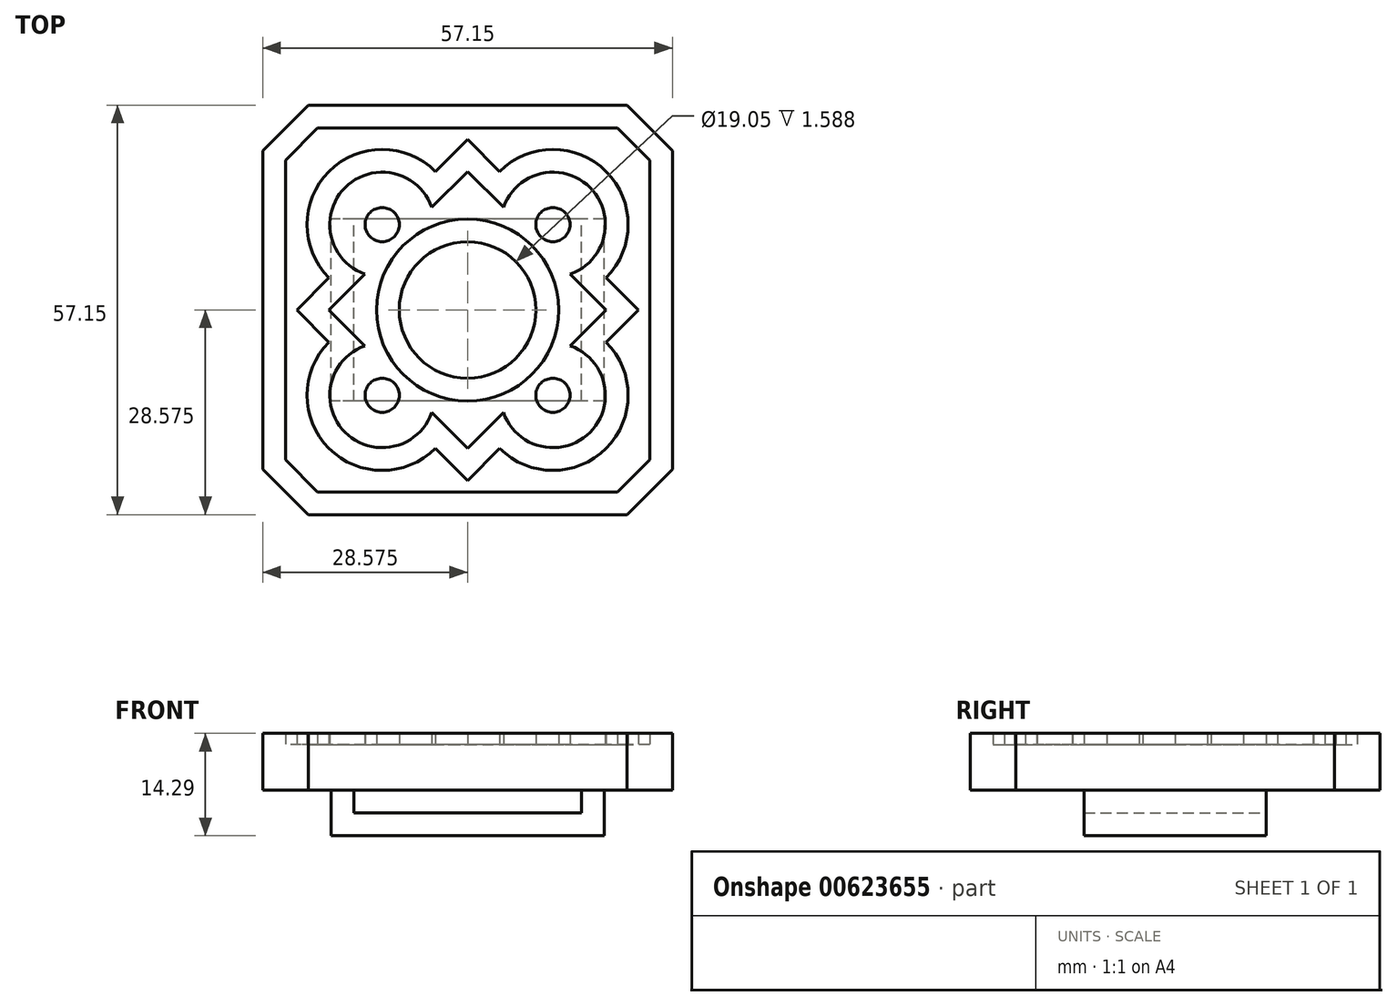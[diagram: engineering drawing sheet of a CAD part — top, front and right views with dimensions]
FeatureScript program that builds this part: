
annotation { "Feature Type Name" : "Feature", "Feature Type Description" : "" }
export const myFeature = defineFeature(function(context is Context, id is Id, definition is map)
    precondition{}
    {
        {
            var Q0;
            Q0=qCreatedBy(makeId("Top.planeOp"),FACE);
            var sketch = newSketch(context, id + "F0", { "sketchPlane" : qUnion([Q0])});
            skLineSegment(sketch, "E0.bottom", {"start": v(-57.15, 0) * mm, "end": v(0, 0) * mm, "construction": true});
            skLineSegment(sketch, "E0.top", {"start": v(-57.15, -57.15) * mm, "end": v(0, -57.15) * mm, "construction": true});
            skLineSegment(sketch, "E0.left", {"start": v(-57.15, 0) * mm, "end": v(-57.15, -57.15) * mm, "construction": true});
            skLineSegment(sketch, "E0.right", {"start": v(0, 0) * mm, "end": v(0, -57.15) * mm, "construction": true});
            skLineSegment(sketch, "E1", {"start": v(-50.8, 0) * mm, "end": v(-6.35, 0) * mm});
            skLineSegment(sketch, "E2", {"start": v(0, -6.35) * mm, "end": v(0, -50.8) * mm});
            skLineSegment(sketch, "E3", {"start": v(-57.15, -6.35) * mm, "end": v(-57.15, -50.8) * mm});
            skLineSegment(sketch, "E4", {"start": v(-50.8, -57.15) * mm, "end": v(-6.35, -57.15) * mm});
            skPoint(sketch, "E5", {"position": v(-28.58, 0) * mm});
            skPoint(sketch, "E6", {"position": v(-57.15, -28.57) * mm});
            skPoint(sketch, "E7", {"position": v(-28.58, -57.15) * mm});
            skPoint(sketch, "E8", {"position": v(0, -28.58) * mm});
            skLineSegment(sketch, "E9", {"start": v(-50.8, -57.15) * mm, "end": v(-57.15, -50.8) * mm});
            skLineSegment(sketch, "E10", {"start": v(0, -50.8) * mm, "end": v(-6.35, -57.15) * mm});
            skLineSegment(sketch, "E11", {"start": v(-57.15, -6.35) * mm, "end": v(-50.8, 0) * mm});
            skLineSegment(sketch, "E12", {"start": v(-6.35, 0) * mm, "end": v(0, -6.35) * mm});
            skLineSegment(sketch, "E13", {"start": v(-28.58, 0) * mm, "end": v(-28.58, -57.15) * mm, "construction": true});
            skPoint(sketch, "E14", {"position": v(-28.58, -28.58) * mm});
            skSolve(sketch);
        }
        {
            var Q0;
            Q0 = qSketchRegion(id + "F0", true);
            extrude(context, id + "F1", {"entities" : qUnion([Q0]), "depth" : 6.35 * mm, "offsetDistance" : 25.4 * mm});
        }
        {
            var Q0;
            Q0=makeQuery(id+"F1.opExtrude","CAP_FACE",FACE,{"disambiguationData":[OSD([sQuery(id+"F0.wireOp",EDGE,"E1"),sQuery(id+"F0.wireOp",EDGE,"E2"),sQuery(id+"F0.wireOp",EDGE,"E3"),sQuery(id+"F0.wireOp",EDGE,"E4"),sQuery(id+"F0.wireOp",EDGE,"E9"),sQuery(id+"F0.wireOp",EDGE,"E10"),sQuery(id+"F0.wireOp",EDGE,"E11"),sQuery(id+"F0.wireOp",EDGE,"E12")])],"isStart":false});
            var sketch = newSketch(context, id + "F2", { "sketchPlane" : qUnion([Q0])});
            skLineSegment(sketch, "E15", {"start": v(0, -28.58) * mm, "end": v(-57.15, -28.58) * mm, "construction": true});
            skCircle(sketch, "E16", {"center": v(-28.58, -28.58) * mm, "radius": 12.7 * mm});
            skCircle(sketch, "E17", {"center": v(-28.58, -28.58) * mm, "radius": 9.53 * mm});
            skLineSegment(sketch, "E18", {"start": v(-6.35, 0) * mm, "end": v(-50.8, 0) * mm});
            skLineSegment(sketch, "E19", {"start": v(0, -50.8) * mm, "end": v(-6.35, -57.15) * mm});
            skLineSegment(sketch, "E20", {"start": v(0, -50.8) * mm, "end": v(0, -6.35) * mm});
            skLineSegment(sketch, "E21", {"start": v(0, -6.35) * mm, "end": v(-6.35, 0) * mm});
            skLineSegment(sketch, "E22", {"start": v(-57.15, -6.35) * mm, "end": v(-50.8, 0) * mm});
            skLineSegment(sketch, "E23", {"start": v(-57.15, -50.8) * mm, "end": v(-50.8, -57.15) * mm});
            skLineSegment(sketch, "E24", {"start": v(-57.15, -6.35) * mm, "end": v(-57.15, -50.8) * mm});
            skLineSegment(sketch, "E25", {"start": v(-6.35, -57.15) * mm, "end": v(-50.8, -57.15) * mm});
            skLineSegment(sketch, "E26", {"start": v(-3.18, -49.48) * mm, "end": v(-3.18, -7.67) * mm});
            skLineSegment(sketch, "E27", {"start": v(-53.97, -49.48) * mm, "end": v(-53.97, -7.67) * mm});
            skLineSegment(sketch, "E28", {"start": v(-49.48, -53.98) * mm, "end": v(-7.67, -53.98) * mm});
            skLineSegment(sketch, "E29", {"start": v(-49.48, -3.17) * mm, "end": v(-7.67, -3.17) * mm});
            skLineSegment(sketch, "E30", {"start": v(-3.17, -7.67) * mm, "end": v(-7.67, -3.18) * mm});
            skLineSegment(sketch, "E31", {"start": v(-49.48, -53.97) * mm, "end": v(-53.97, -49.48) * mm});
            skLineSegment(sketch, "E32", {"start": v(-7.67, -53.97) * mm, "end": v(-3.17, -49.48) * mm});
            skLineSegment(sketch, "E33", {"start": v(-53.97, -7.67) * mm, "end": v(-49.48, -3.18) * mm});
            skLineSegment(sketch, "E34", {"start": v(-28.58, -53.98) * mm, "end": v(-28.58, -3.18) * mm, "construction": true});
            skLineSegment(sketch, "E35", {"start": v(-3.17, -3.18) * mm, "end": v(-53.98, -53.98) * mm, "construction": true});
            skLineSegment(sketch, "E36", {"start": v(-53.98, -3.17) * mm, "end": v(-3.17, -53.98) * mm, "construction": true});
            skLineSegment(sketch, "E37", {"start": v(-4.76, -28.58) * mm, "end": v(-28.58, -4.76) * mm, "construction": true});
            skLineSegment(sketch, "E38", {"start": v(-4.76, -28.57) * mm, "end": v(-28.57, -52.39) * mm, "construction": true});
            skLineSegment(sketch, "E39", {"start": v(-28.57, -52.39) * mm, "end": v(-52.39, -28.58) * mm, "construction": true});
            skLineSegment(sketch, "E40", {"start": v(-28.58, -4.76) * mm, "end": v(-52.39, -28.57) * mm, "construction": true});
            skCircle(sketch, "E41", {"center": v(-16.67, -40.48) * mm, "radius": 2.38 * mm});
            skCircle(sketch, "E42", {"center": v(-40.48, -40.48) * mm, "radius": 2.38 * mm});
            skCircle(sketch, "E43", {"center": v(-16.67, -16.67) * mm, "radius": 2.38 * mm});
            skCircle(sketch, "E44", {"center": v(-40.48, -16.67) * mm, "radius": 2.38 * mm});
            skLineSegment(sketch, "E45", {"start": v(-47.9, -28.58) * mm, "end": v(-28.58, -47.9) * mm, "construction": true});
            skLineSegment(sketch, "E46", {"start": v(-47.9, -28.58) * mm, "end": v(-28.58, -9.25) * mm, "construction": true});
            skLineSegment(sketch, "E47", {"start": v(-28.58, -9.25) * mm, "end": v(-9.25, -28.57) * mm, "construction": true});
            skLineSegment(sketch, "E48", {"start": v(-9.25, -28.57) * mm, "end": v(-28.58, -47.9) * mm, "construction": true});
            skArc(sketch, "E49", {"start": v(-24.08, -47.9) * mm, "mid": v(-9.25, -47.9) * mm, "end": v(-9.25, -33.07) * mm});
            skLineSegment(sketch, "E50", {"start": v(-9.25, -33.07) * mm, "end": v(-24.08, -47.9) * mm, "construction": true});
            skArc(sketch, "E51", {"start": v(-47.9, -33.07) * mm, "mid": v(-47.9, -47.9) * mm, "end": v(-33.07, -47.9) * mm});
            skArc(sketch, "E52", {"start": v(-33.07, -9.25) * mm, "mid": v(-47.9, -9.25) * mm, "end": v(-47.9, -24.08) * mm});
            skArc(sketch, "E53", {"start": v(-9.25, -24.08) * mm, "mid": v(-9.25, -9.25) * mm, "end": v(-24.08, -9.25) * mm});
            skLineSegment(sketch, "E54", {"start": v(-24.08, -47.9) * mm, "end": v(-28.57, -52.39) * mm});
            skLineSegment(sketch, "E55", {"start": v(-28.57, -52.39) * mm, "end": v(-33.07, -47.9) * mm});
            skLineSegment(sketch, "E56", {"start": v(-47.9, -33.07) * mm, "end": v(-52.39, -28.58) * mm});
            skLineSegment(sketch, "E57", {"start": v(-52.39, -28.58) * mm, "end": v(-47.9, -24.08) * mm});
            skLineSegment(sketch, "E58", {"start": v(-33.07, -9.25) * mm, "end": v(-28.58, -4.76) * mm});
            skLineSegment(sketch, "E59", {"start": v(-24.08, -9.25) * mm, "end": v(-28.58, -4.76) * mm});
            skLineSegment(sketch, "E60", {"start": v(-9.25, -24.08) * mm, "end": v(-4.76, -28.57) * mm});
            skLineSegment(sketch, "E61", {"start": v(-9.25, -33.07) * mm, "end": v(-4.76, -28.57) * mm});
            skArc(sketch, "E62", {"start": v(-14.26, -23.57) * mm, "mid": v(-11.5, -11.5) * mm, "end": v(-23.57, -14.26) * mm});
            skArc(sketch, "E63", {"start": v(-23.57, -42.9) * mm, "mid": v(-11.5, -45.65) * mm, "end": v(-14.26, -33.58) * mm});
            skArc(sketch, "E64", {"start": v(-42.9, -33.58) * mm, "mid": v(-45.65, -45.65) * mm, "end": v(-33.58, -42.9) * mm});
            skArc(sketch, "E65", {"start": v(-33.58, -14.26) * mm, "mid": v(-45.65, -11.5) * mm, "end": v(-42.9, -23.57) * mm});
            skLineSegment(sketch, "E66", {"start": v(-33.58, -42.9) * mm, "end": v(-28.58, -47.9) * mm});
            skLineSegment(sketch, "E67", {"start": v(-28.57, -47.9) * mm, "end": v(-23.57, -42.9) * mm});
            skLineSegment(sketch, "E68", {"start": v(-14.26, -33.58) * mm, "end": v(-9.25, -28.57) * mm});
            skLineSegment(sketch, "E69", {"start": v(-9.25, -28.57) * mm, "end": v(-14.26, -23.57) * mm});
            skLineSegment(sketch, "E70", {"start": v(-23.57, -14.26) * mm, "end": v(-28.58, -9.25) * mm});
            skLineSegment(sketch, "E71", {"start": v(-33.58, -14.26) * mm, "end": v(-28.58, -9.25) * mm});
            skLineSegment(sketch, "E72", {"start": v(-42.9, -23.57) * mm, "end": v(-47.9, -28.58) * mm});
            skLineSegment(sketch, "E73", {"start": v(-42.9, -33.58) * mm, "end": v(-47.9, -28.58) * mm});
            skSolve(sketch);
        }
        {
            var Q0;
            Q0 = qSketchRegion(id + "F2", true);
            var Q1;
            Q1=makeQuery(id+"F2.imprint","IMPRINT",FACE,{"disambiguationData":[TD([[makeQuery(id+"F2.imprint","IMPRINT",EDGE,{"derivedFrom":sQuery(id+"F2.wireOp",EDGE,"E49")}),1.0]])]});
            var Q2;
            Q2=makeQuery(id+"F2.imprint","IMPRINT",FACE,{"disambiguationData":[TD([[makeQuery(id+"F2.imprint","IMPRINT",EDGE,{"derivedFrom":sQuery(id+"F2.wireOp",EDGE,"E16")}),1.0]])]});
            var Q3;
            Q3=makeQuery(id+"F2.imprint","IMPRINT",FACE,{"disambiguationData":[TD([[makeQuery(id+"F2.imprint","IMPRINT",EDGE,{"derivedFrom":sQuery(id+"F2.wireOp",EDGE,"E42")}),1.0]])]});
            var Q4;
            Q4=makeQuery(id+"F2.imprint","IMPRINT",FACE,{"disambiguationData":[TD([[makeQuery(id+"F2.imprint","IMPRINT",EDGE,{"derivedFrom":sQuery(id+"F2.wireOp",EDGE,"E41")}),1.0]])]});
            var Q5;
            Q5=makeQuery(id+"F2.imprint","IMPRINT",FACE,{"disambiguationData":[TD([[makeQuery(id+"F2.imprint","IMPRINT",EDGE,{"derivedFrom":sQuery(id+"F2.wireOp",EDGE,"E43")}),1.0]])]});
            var Q6;
            Q6=makeQuery(id+"F2.imprint","IMPRINT",FACE,{"disambiguationData":[TD([[makeQuery(id+"F2.imprint","IMPRINT",EDGE,{"derivedFrom":sQuery(id+"F2.wireOp",EDGE,"E44")}),1.0]])]});
            extrude(context, id + "F3", {"entities" : qUnion([Q0, Q1, Q2, Q3, Q4, Q5, Q6]), "operationType" : NewBodyOperationType.ADD, "depth" : 1.59 * mm, "offsetDistance" : 25.4 * mm});
        }
        {
            var Q0;
            Q0=makeQuery(id+"F1.opExtrude","CAP_FACE",FACE,{"disambiguationData":[OSD([sQuery(id+"F0.wireOp",EDGE,"E1"),sQuery(id+"F0.wireOp",EDGE,"E2"),sQuery(id+"F0.wireOp",EDGE,"E3"),sQuery(id+"F0.wireOp",EDGE,"E4"),sQuery(id+"F0.wireOp",EDGE,"E9"),sQuery(id+"F0.wireOp",EDGE,"E10"),sQuery(id+"F0.wireOp",EDGE,"E11"),sQuery(id+"F0.wireOp",EDGE,"E12")])],"isStart":true});
            var sketch = newSketch(context, id + "F4", { "sketchPlane" : qUnion([Q0])});
            skLineSegment(sketch, "E74", {"start": v(0, 28.58) * mm, "end": v(-57.15, 28.58) * mm, "construction": true});
            skLineSegment(sketch, "E75.bottom", {"start": v(-44.45, 41.27) * mm, "end": v(-47.63, 41.27) * mm});
            skLineSegment(sketch, "E75.top", {"start": v(-44.45, 15.88) * mm, "end": v(-47.63, 15.88) * mm});
            skLineSegment(sketch, "E75.left", {"start": v(-44.45, 41.27) * mm, "end": v(-44.45, 15.88) * mm});
            skLineSegment(sketch, "E75.right", {"start": v(-47.63, 41.27) * mm, "end": v(-47.63, 15.88) * mm});
            skLineSegment(sketch, "E76.bottom", {"start": v(-9.53, 41.27) * mm, "end": v(-12.7, 41.27) * mm});
            skLineSegment(sketch, "E76.top", {"start": v(-9.53, 15.88) * mm, "end": v(-12.7, 15.88) * mm});
            skLineSegment(sketch, "E76.left", {"start": v(-9.53, 41.28) * mm, "end": v(-9.53, 15.88) * mm});
            skLineSegment(sketch, "E76.right", {"start": v(-12.7, 41.27) * mm, "end": v(-12.7, 15.88) * mm});
            skLineSegment(sketch, "E77", {"start": v(-9.53, 28.58) * mm, "end": v(-47.63, 28.57) * mm, "construction": true});
            skPoint(sketch, "E78", {"position": v(-28.57, 28.58) * mm});
            skSolve(sketch);
        }
        {
            var Q0;
            Q0 = qSketchRegion(id + "F4", true);
            extrude(context, id + "F5", {"entities" : qUnion([Q0]), "operationType" : NewBodyOperationType.ADD, "depth" : 3.17 * mm, "offsetDistance" : 25.4 * mm});
        }
        {
            var Q0;
            Q0=makeQuery(id+"F5.opExtrude","CAP_FACE",FACE,{"disambiguationData":[OSD([sQuery(id+"F4.wireOp",EDGE,"E76.bottom"),sQuery(id+"F4.wireOp",EDGE,"E76.top"),sQuery(id+"F4.wireOp",EDGE,"E76.left"),sQuery(id+"F4.wireOp",EDGE,"E76.right")])],"isStart":false});
            var sketch = newSketch(context, id + "F6", { "sketchPlane" : qUnion([Q0])});
            skLineSegment(sketch, "E79.bottom", {"start": v(-9.53, 41.27) * mm, "end": v(-47.63, 41.27) * mm});
            skLineSegment(sketch, "E79.top", {"start": v(-9.52, 15.88) * mm, "end": v(-47.63, 15.88) * mm});
            skLineSegment(sketch, "E79.left", {"start": v(-9.53, 41.27) * mm, "end": v(-9.52, 15.88) * mm});
            skLineSegment(sketch, "E79.right", {"start": v(-47.63, 41.27) * mm, "end": v(-47.63, 15.88) * mm});
            skSolve(sketch);
        }
        {
            var Q0;
            Q0 = qSketchRegion(id + "F6", true);
            extrude(context, id + "F7", {"entities" : qUnion([Q0]), "operationType" : NewBodyOperationType.ADD, "depth" : 3.17 * mm, "offsetDistance" : 25.4 * mm});
        }
    });
